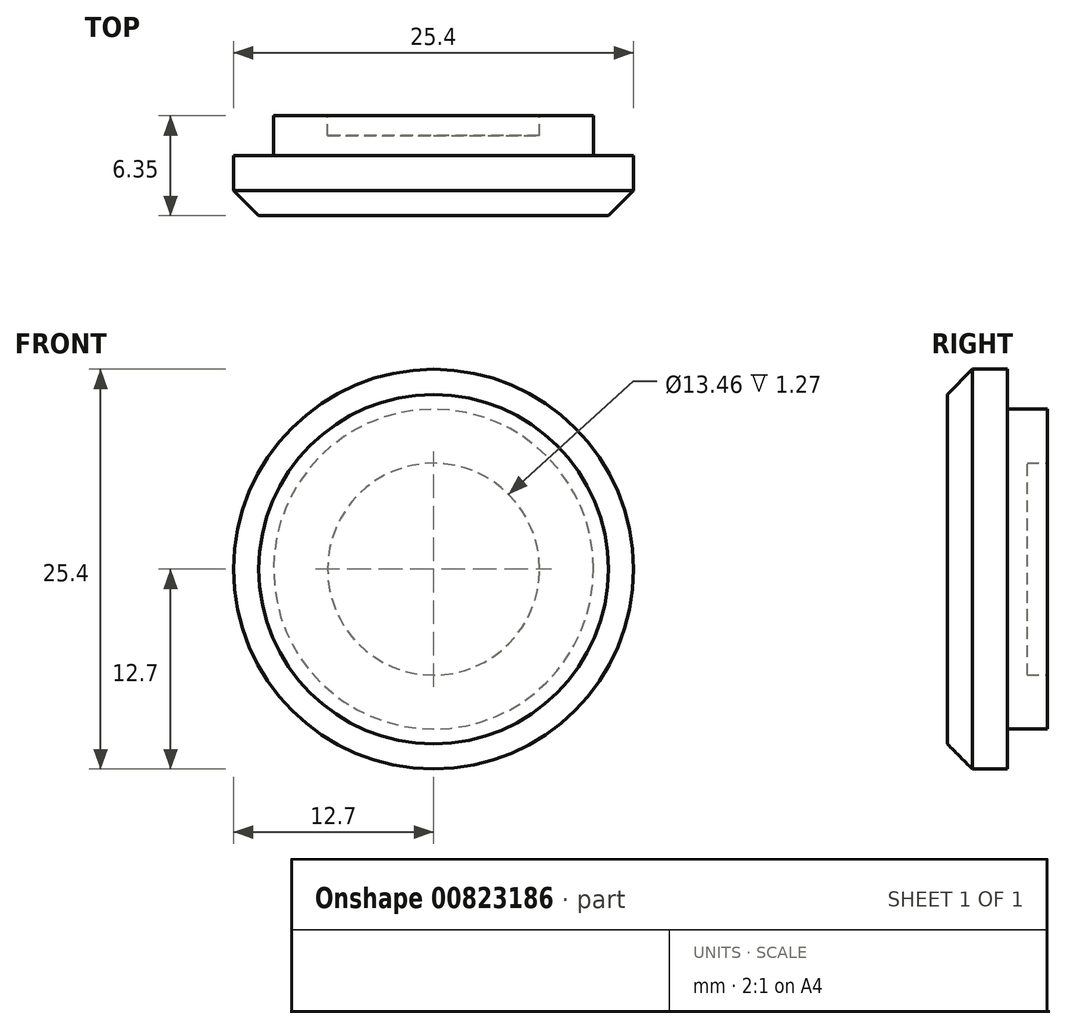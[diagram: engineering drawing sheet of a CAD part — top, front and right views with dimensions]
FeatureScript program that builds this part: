
annotation { "Feature Type Name" : "Feature", "Feature Type Description" : "" }
export const myFeature = defineFeature(function(context is Context, id is Id, definition is map)
    precondition{}
    {
        {
            var Q0;
            Q0=qCreatedBy(makeId("Front.planeOp"),FACE);
            var sketch = newSketch(context, id + "F0", { "sketchPlane" : qUnion([Q0])});
            skCircle(sketch, "E0", {"center": v(0, 0) * mm, "radius": 12.7 * mm});
            skCircle(sketch, "E1", {"center": v(0, 0) * mm, "radius": 10.16 * mm});
            skCircle(sketch, "E2", {"center": v(0, 0) * mm, "radius": 6.73 * mm});
            skSolve(sketch);
        }
        {
            var Q0;
            Q0 = qSketchRegion(id + "F0", true);
            var Q1;
            Q1=makeQuery(id+"F0.imprint","IMPRINT",FACE,{"disambiguationData":[TD([[makeQuery(id+"F0.imprint","IMPRINT",EDGE,{"derivedFrom":sQuery(id+"F0.wireOp",EDGE,"E1")}),1.0]])]});
            var Q2;
            Q2=makeQuery(id+"F0.imprint","IMPRINT",FACE,{"disambiguationData":[TD([[makeQuery(id+"F0.imprint","IMPRINT",EDGE,{"derivedFrom":sQuery(id+"F0.wireOp",EDGE,"E2")}),1.0]])]});
            extrude(context, id + "F1", {"entities" : qUnion([Q0, Q1, Q2]), "depth" : 6.35 * mm, "offsetDistance" : 25.4 * mm});
        }
        {
            var Q0;
            Q0=makeQuery(id+"F0.imprint","IMPRINT",FACE,{"disambiguationData":[TD([[makeQuery(id+"F0.imprint","IMPRINT",EDGE,{"derivedFrom":sQuery(id+"F0.wireOp",EDGE,"E0")}),1.0]])]});
            extrude(context, id + "F2", {"entities" : qUnion([Q0]), "operationType" : NewBodyOperationType.REMOVE, "oppositeDirection" : true, "depth" : -2.54 * mm, "offsetDistance" : 25.4 * mm});
        }
        {
            var Q0;
            Q0=makeQuery(id+"F0.imprint","IMPRINT",FACE,{"disambiguationData":[TD([[makeQuery(id+"F0.imprint","IMPRINT",EDGE,{"derivedFrom":sQuery(id+"F0.wireOp",EDGE,"E2")}),1.0]])]});
            extrude(context, id + "F3", {"entities" : qUnion([Q0]), "operationType" : NewBodyOperationType.REMOVE, "oppositeDirection" : true, "depth" : -1.27 * mm, "offsetDistance" : 25.4 * mm});
        }
        {
            var Q0;
            Q0=makeQuery(id+"F1.opExtrude","CAP_EDGE",EDGE,{"disambiguationData":[OSD([sQuery(id+"F0.wireOp",EDGE,"E0")])],"isStart":false});
            chamfer(context, id + "F4", {"entities" : qUnion([Q0]), "width" : 1.6 * mm, "tangentPropagation" : true});
        }
    });
